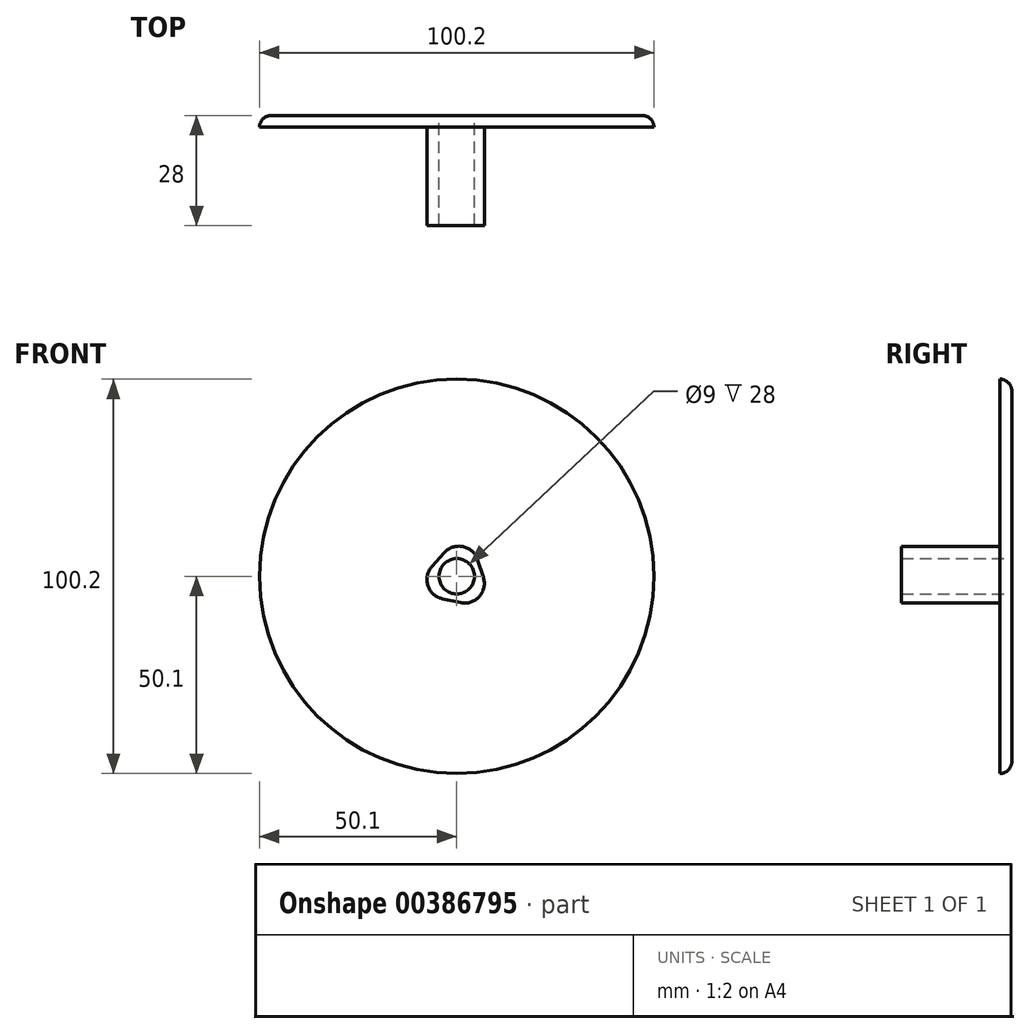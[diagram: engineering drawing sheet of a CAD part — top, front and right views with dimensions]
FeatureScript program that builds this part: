
annotation { "Feature Type Name" : "Feature", "Feature Type Description" : "" }
export const myFeature = defineFeature(function(context is Context, id is Id, definition is map)
    precondition{}
    {
        {
            var Q0;
            Q0=qCreatedBy(makeId("Front.planeOp"),FACE);
            var sketch = newSketch(context, id + "F0", { "sketchPlane" : qUnion([Q0])});
            skCircle(sketch, "E0", {"center": v(0, 0) * mm, "radius": 50.1 * mm});
            skCircle(sketch, "E1", {"center": v(0, 0) * mm, "radius": 4.5 * mm});
            skSolve(sketch);
        }
        {
            var Q0;
            Q0 = qSketchRegion(id + "F0", true);
            extrude(context, id + "F1", {"entities" : qUnion([Q0]), "depth" : 3 * mm});
        }
        {
            var Q0;
            Q0=makeQuery(id+"F1.opExtrude","CAP_FACE",FACE,{"disambiguationData":[OSD([sQuery(id+"F0.wireOp",EDGE,"E0"),sQuery(id+"F0.wireOp",EDGE,"E1")])],"isStart":false});
            var sketch = newSketch(context, id + "F2", { "sketchPlane" : qUnion([Q0])});
            skCircle(sketch, "E2.cCircle", {"center": v(0, 0) * mm, "radius": 6.35 * mm, "construction": true});
            skLineSegment(sketch, "E2.0", {"start": v(2.6, 12.43) * mm, "end": v(9.47, -8.47) * mm});
            skLineSegment(sketch, "E2.1", {"start": v(9.47, -8.47) * mm, "end": v(-12.07, -3.97) * mm});
            skLineSegment(sketch, "E2.2", {"start": v(-12.07, -3.97) * mm, "end": v(2.6, 12.43) * mm});
            skPoint(sketch, "E2.0.midPoint", {"position": v(6.03, 1.98) * mm});
            skCircle(sketch, "E3", {"center": v(0, 0) * mm, "radius": 4.5 * mm});
            skSolve(sketch);
        }
        {
            var Q0;
            Q0 = qSketchRegion(id + "F2", true);
            extrude(context, id + "F3", {"entities" : qUnion([Q0]), "operationType" : NewBodyOperationType.ADD, "depth" : 25 * mm});
        }
        {
            var Q0;
            Q0=makeQuery(id+"F1.opExtrude","CAP_EDGE",EDGE,{"disambiguationData":[OSD([sQuery(id+"F0.wireOp",EDGE,"E0")])],"isStart":true});
            fillet(context, id + "F4", {"entities" : qUnion([Q0]), "radius" : 3 * mm, "tangentPropagation" : true, "allowEdgeOverflow" : false});
        }
        {
            var Q0;
            Q0=makeQuery(id+"F3.opExtrude","SWEPT_EDGE",EDGE,{"disambiguationData":[OSD([sQuery(id+"F2.wireOp",EDGE,"E2.0"),sQuery(id+"F2.wireOp",EDGE,"E2.2")])]});
            var Q1;
            Q1=makeQuery(id+"F3.opExtrude","SWEPT_EDGE",EDGE,{"disambiguationData":[OSD([sQuery(id+"F2.wireOp",EDGE,"E2.1"),sQuery(id+"F2.wireOp",EDGE,"E2.2")])]});
            var Q2;
            Q2=makeQuery(id+"F3.opExtrude","SWEPT_EDGE",EDGE,{"disambiguationData":[OSD([sQuery(id+"F2.wireOp",EDGE,"E2.0"),sQuery(id+"F2.wireOp",EDGE,"E2.1")])]});
            fillet(context, id + "F5", {"entities" : qUnion([Q0, Q1, Q2]), "radius" : 5 * mm, "tangentPropagation" : true, "allowEdgeOverflow" : false});
        }
    });
